# Revit family: Doors_IntSgl
name_source: partatom
category: Doors
revit_build: Autodesk Revit 2015 (Build: 20160512_1515(x64)
units: mm (PartAtom-declared; Revit-internal decimal feet)

## types (3) — shared parameters
Analytic Construction = Metal
Architrave Setback = 5 mm  [stored 0.0164042 ft]
Description = Internal Single Door
Door Panel Height = 2060 mm
Door Panel Thickness = 38 mm  [stored 0.124672 ft]
Frame Thickness = 32 mm  [stored 0.104987 ft]
Function = Interior
Handle X Distance = 75 mm  [stored 0.246063 ft]
Heat Transfer Coefficient (U) = 3.7021 W/(m²·K)
Height = 2110 mm  [stored 6.92257 ft]
Height to Top Lock Rail = 1000 mm  [stored 3.28084 ft]
Keynote = L20
Manufacturer = Revit
Material Architrave = Door - Architrave
Material Door = Door - Panel
Material Frame = Door - Frame/Mullion (1)
Material Ironmongery = Door - Handle
Operation = SingleSwingRight
Rough Height = 2110 mm  [stored 6.92257 ft]
Stop Thickness = 19 mm  [stored 0.062336 ft]
StopDepth = 32 mm  [stored 0.104987 ft]
Structural Tolerance = 8 mm  [stored 0.0262467 ft]
Thermal Resistance (R) = 0.2701 (m²·K)/W
Thickness = 38 mm  [stored 0.124672 ft]
Tolerance = 2 mm  [stored 0.00656168 ft]
Type Comments = Internal Single
UnderCut = 8 mm  [stored 0.0262467 ft]
Vis - Ironmongery = Yes
Wall Closure = By host
zero-valued in all types: Door Panel Offset, Solar Heat Gain Coefficient, Visual Light Transmittance

## per-type parameters (varying)
| type | Door Panel Width | Handle Z Distance | Rough Width | Width |
| 1010x2110mm | 926 mm | 900 mm  [stored 2.95276 ft] | 1010 mm  [stored 3.31365 ft] | 1010 mm  [stored 3.31365 ft] |
| 810x2110mm | 726 mm | 900 mm  [stored 2.95276 ft] | 810 mm | 810 mm |
| 910x2110mm | 826 mm | 1000 mm  [stored 3.28084 ft] | 910 mm | 910 mm |

note: [stored X ft] marks values corroborated as IEEE doubles in the binary element streams (Revit-internal decimal feet)

## geometry (parser evidence)
native form markers: Blend x10, Sweep x4
no freeform markers — native parametric forms only
